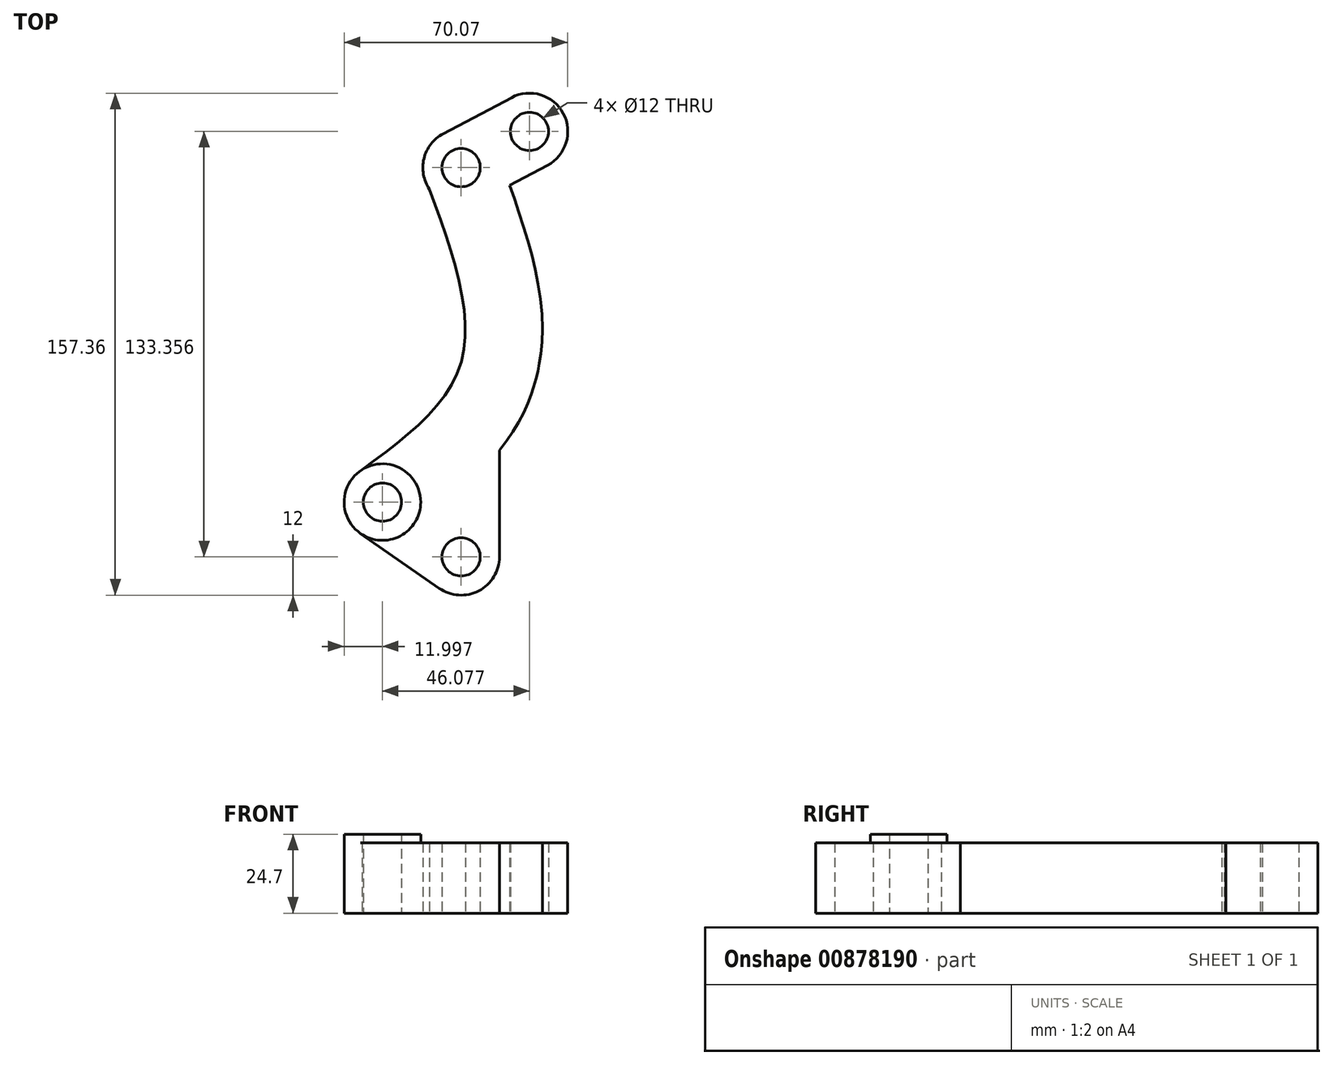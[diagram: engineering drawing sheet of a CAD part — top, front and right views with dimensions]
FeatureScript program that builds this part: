
annotation { "Feature Type Name" : "Feature", "Feature Type Description" : "" }
export const myFeature = defineFeature(function(context is Context, id is Id, definition is map)
    precondition{}
    {
        {
            var Q0;
            Q0=qCreatedBy(makeId("Top.planeOp"),FACE);
            var sketch = newSketch(context, id + "F0", { "sketchPlane" : qUnion([Q0])});
            skCircle(sketch, "E0", {"center": v(0, 0) * mm, "radius": 73.5 * mm, "construction": true});
            skCircle(sketch, "E1", {"center": v(0, 0) * mm, "radius": 70 * mm, "construction": true});
            skCircle(sketch, "E2", {"center": v(-34.34, 61) * mm, "radius": 6 * mm});
            skCircle(sketch, "E3", {"center": v(-34.34, -61) * mm, "radius": 6 * mm});
            skCircle(sketch, "E4", {"center": v(-59, -43.84) * mm, "radius": 6 * mm});
            skCircle(sketch, "E5", {"center": v(-12.92, 72.36) * mm, "radius": 6 * mm});
            skLineSegment(sketch, "E6", {"start": v(-12.92, 72.36) * mm, "end": v(-59, -43.84) * mm, "construction": true});
            skLineSegment(sketch, "E7", {"start": v(-34.34, 61) * mm, "end": v(-34.34, -61) * mm, "construction": true});
            skCircle(sketch, "E8", {"center": v(-59, -43.84) * mm, "radius": 12 * mm});
            skCircle(sketch, "E9", {"center": v(-34.34, -61) * mm, "radius": 12 * mm});
            skCircle(sketch, "E10", {"center": v(-12.92, 72.36) * mm, "radius": 12 * mm});
            skCircle(sketch, "E11", {"center": v(-34.34, 61) * mm, "radius": 12 * mm});
            skLineSegment(sketch, "E12", {"start": v(-34.34, -61) * mm, "end": v(-22.34, -61) * mm});
            skLineSegment(sketch, "E13", {"start": v(-22.34, -61) * mm, "end": v(-22.34, 51.12) * mm});
            skPoint(sketch, "E14.visualSharp", {"position": v(-22.34, 53.62) * mm});
            skPoint(sketch, "E15.start.orphan", {"position": v(-22.34, 61) * mm});
            skLineSegment(sketch, "E16", {"start": v(-28.72, 50.4) * mm, "end": v(-5.82, 62.54) * mm});
            skLineSegment(sketch, "E17", {"start": v(-65.85, -53.7) * mm, "end": v(-41.2, -70.85) * mm});
            skLineSegment(sketch, "E18", {"start": v(-70.7, -41.22) * mm, "end": v(-70.67, -41.1) * mm});
            skLineSegment(sketch, "E19.trimOffspring", {"start": v(-39.96, 71.6) * mm, "end": v(-18.54, 82.96) * mm});
            skArc(sketch, "E20.trimOffspring", {"start": v(-21.05, 54.46) * mm, "mid": v(-22, 52.9) * mm, "end": v(-22.34, 51.12) * mm});
            skFitSpline(sketch, "E21", {"points": [v(-44.25, 54.24) * mm, v(-34.34, 0) * mm, v(-65.34, -33.66) * mm], "startDerivative": vector(40.92, -112.3) * mm, "endDerivative": vector(-85.05, -62.73) * mm});
            skFitSpline(sketch, "E22.0", {"points": [v(-21.7, 62.46) * mm, v(-20.85, 60.12) * mm, v(-19.1, 55.34) * mm, v(-16.51, 47.93) * mm, v(-14.06, 40.28) * mm, v(-11.88, 32.38) * mm, v(-10.14, 24.17) * mm, v(-9.04, 15.58) * mm, v(-8.9, 8.03) * mm, v(-9.4, 2.54) * mm, v(-9.88, -0.65) * mm, v(-10.35, -3.06) * mm, v(-10.93, -5.48) * mm, v(-11.64, -7.92) * mm, v(-12.44, -10.28) * mm, v(-13.64, -13.33) * mm, v(-15.35, -16.96) * mm, v(-17.65, -21) * mm, v(-20.16, -24.73) * mm, v(-23.7, -29.33) * mm, v(-28.37, -34.45) * mm, v(-34.15, -39.82) * mm, v(-39.96, -44.6) * mm, v(-45.67, -48.97) * mm, v(-49.32, -51.67) * mm, v(-51.1, -52.97) * mm]});
            skSolve(sketch);
        }
        {
            var Q0;
            Q0=makeQuery(id+"F0.imprint","IMPRINT",FACE,{"disambiguationData":[TD([[makeQuery(id+"F0.imprint","IMPRINT",EDGE,{"derivedFrom":sQuery(id+"F0.wireOp",EDGE,"E2")}),-1.0]])]});
            var Q1;
            Q1=makeQuery(id+"F0.imprint","IMPRINT",FACE,{"disambiguationData":[TD([[makeQuery(id+"F0.imprint","IMPRINT",EDGE,{"derivedFrom":sQuery(id+"F0.wireOp",EDGE,"E3")}),-1.0]])]});
            var Q2;
            {var subQ0=sQuery(id+"F0.wireOp",EDGE,"uvAYMqGV-DIzJ-fmoX-Jquh-CrT9dVzAXWpi");Q2=makeQuery(id+"F0.imprint","IMPRINT",FACE,{"disambiguationData":[TD([[makeQuery(id+"F0.imprint","IMPRINT",EDGE,{"derivedFrom":subQ0}),1.0]])]});}
            var Q3;
            Q3=makeQuery(id+"F0.imprint","IMPRINT",FACE,{"disambiguationData":[TD([[makeQuery(id+"F0.imprint","IMPRINT",EDGE,{"derivedFrom":sQuery(id+"F0.wireOp",EDGE,"E5")}),-1.0]])]});
            var Q4;
            {var subQ0=sQuery(id+"F0.wireOp",EDGE,"E20.trimOffspring");Q4=makeQuery(id+"F0.imprint","IMPRINT",FACE,{"disambiguationData":[TD([[makeQuery(id+"F0.imprint","IMPRINT",EDGE,{"derivedFrom":subQ0}),1.0]])]});}
            var Q5;
            {var subQ8=sQuery(id+"F0.wireOp",EDGE,"E17");Q5=makeQuery(id+"F0.imprint","IMPRINT",FACE,{"disambiguationData":[TD([[makeQuery(id+"F0.imprint","IMPRINT",EDGE,{"derivedFrom":subQ8}),1.0]])]});}
            var Q6;
            {var subQ5=sQuery(id+"F0.wireOp",EDGE,"E19.trimOffspring");Q6=makeQuery(id+"F0.imprint","IMPRINT",FACE,{"disambiguationData":[TD([[makeQuery(id+"F0.imprint","IMPRINT",EDGE,{"derivedFrom":subQ5}),-1.0]])]});}
            extrude(context, id + "F1", {"entities" : qUnion([Q0, Q1, Q2, Q3, Q4, Q5, Q6]), "depth" : 22 * mm, "offsetDistance" : 25 * mm});
        }
        {
            var Q0;
            Q0=makeQuery(id+"F0.imprint","IMPRINT",FACE,{"disambiguationData":[TD([[makeQuery(id+"F0.imprint","IMPRINT",EDGE,{"derivedFrom":sQuery(id+"F0.wireOp",EDGE,"E4")}),-1.0]])]});
            extrude(context, id + "F2", {"entities" : qUnion([Q0]), "operationType" : NewBodyOperationType.ADD, "depth" : 24.7 * mm, "offsetDistance" : 25 * mm});
        }
    });
